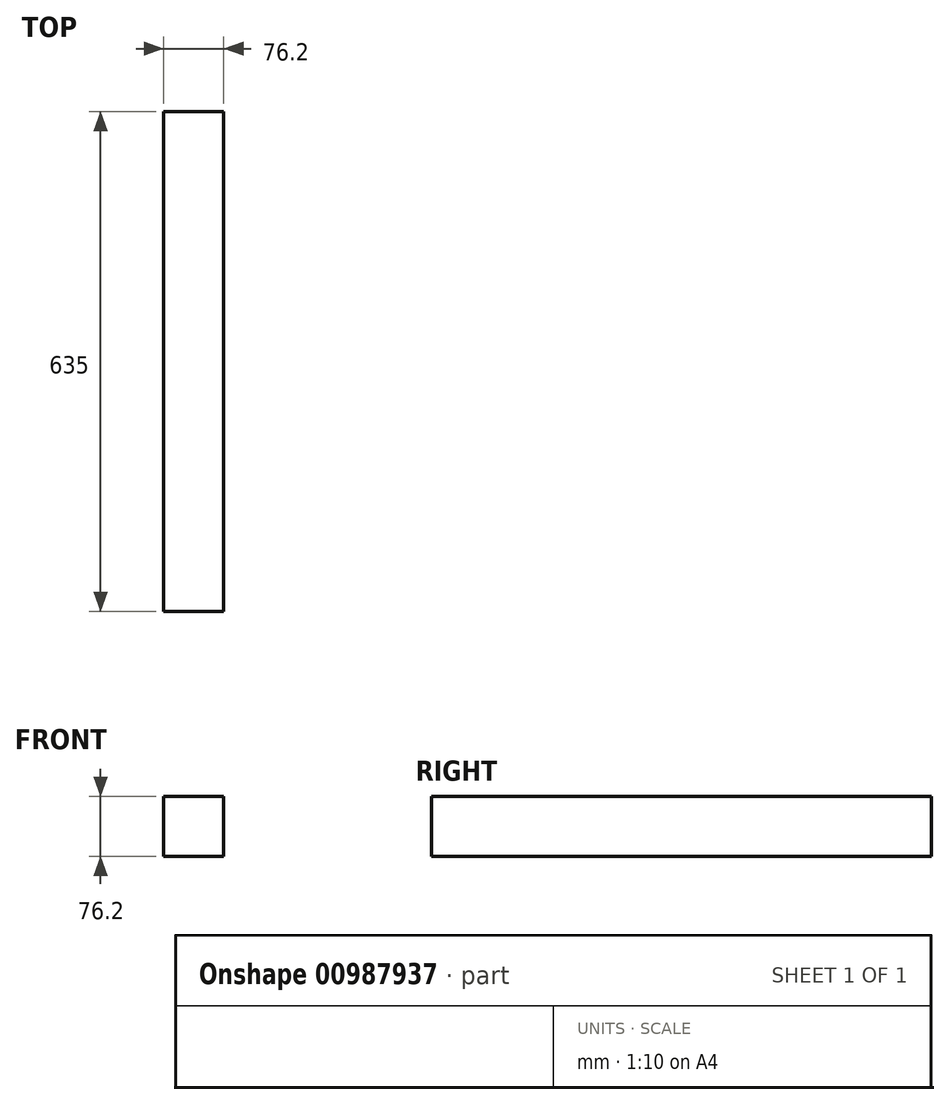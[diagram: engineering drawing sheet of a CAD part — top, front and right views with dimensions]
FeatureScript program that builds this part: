
annotation { "Feature Type Name" : "Feature", "Feature Type Description" : "" }
export const myFeature = defineFeature(function(context is Context, id is Id, definition is map)
    precondition{}
    {
        {
            var Q0;
            Q0=qCreatedBy(makeId("Front.planeOp"),FACE);
            var sketch = newSketch(context, id + "F0", { "sketchPlane" : qUnion([Q0])});
            skLineSegment(sketch, "E0.bottom", {"start": v(-101.43, 109.31) * mm, "end": v(-25.23, 109.31) * mm});
            skLineSegment(sketch, "E0.top", {"start": v(-101.43, 33.11) * mm, "end": v(-25.23, 33.11) * mm});
            skLineSegment(sketch, "E0.left", {"start": v(-101.43, 109.31) * mm, "end": v(-101.43, 33.11) * mm});
            skLineSegment(sketch, "E0.right", {"start": v(-25.23, 109.31) * mm, "end": v(-25.23, 33.11) * mm});
            skSolve(sketch);
        }
        {
            var Q0;
            Q0=makeQuery(id+"F0.imprint","IMPRINT",FACE,{"disambiguationData":[TD([[makeQuery(id+"F0.imprint","IMPRINT",EDGE,{"derivedFrom":sQuery(id+"F0.wireOp",EDGE,"E0.bottom")}),-1.0]])]});
            extrude(context, id + "F1", {"entities" : qUnion([Q0]), "depth" : 635 * mm, "offsetDistance" : 25.4 * mm});
        }
    });
